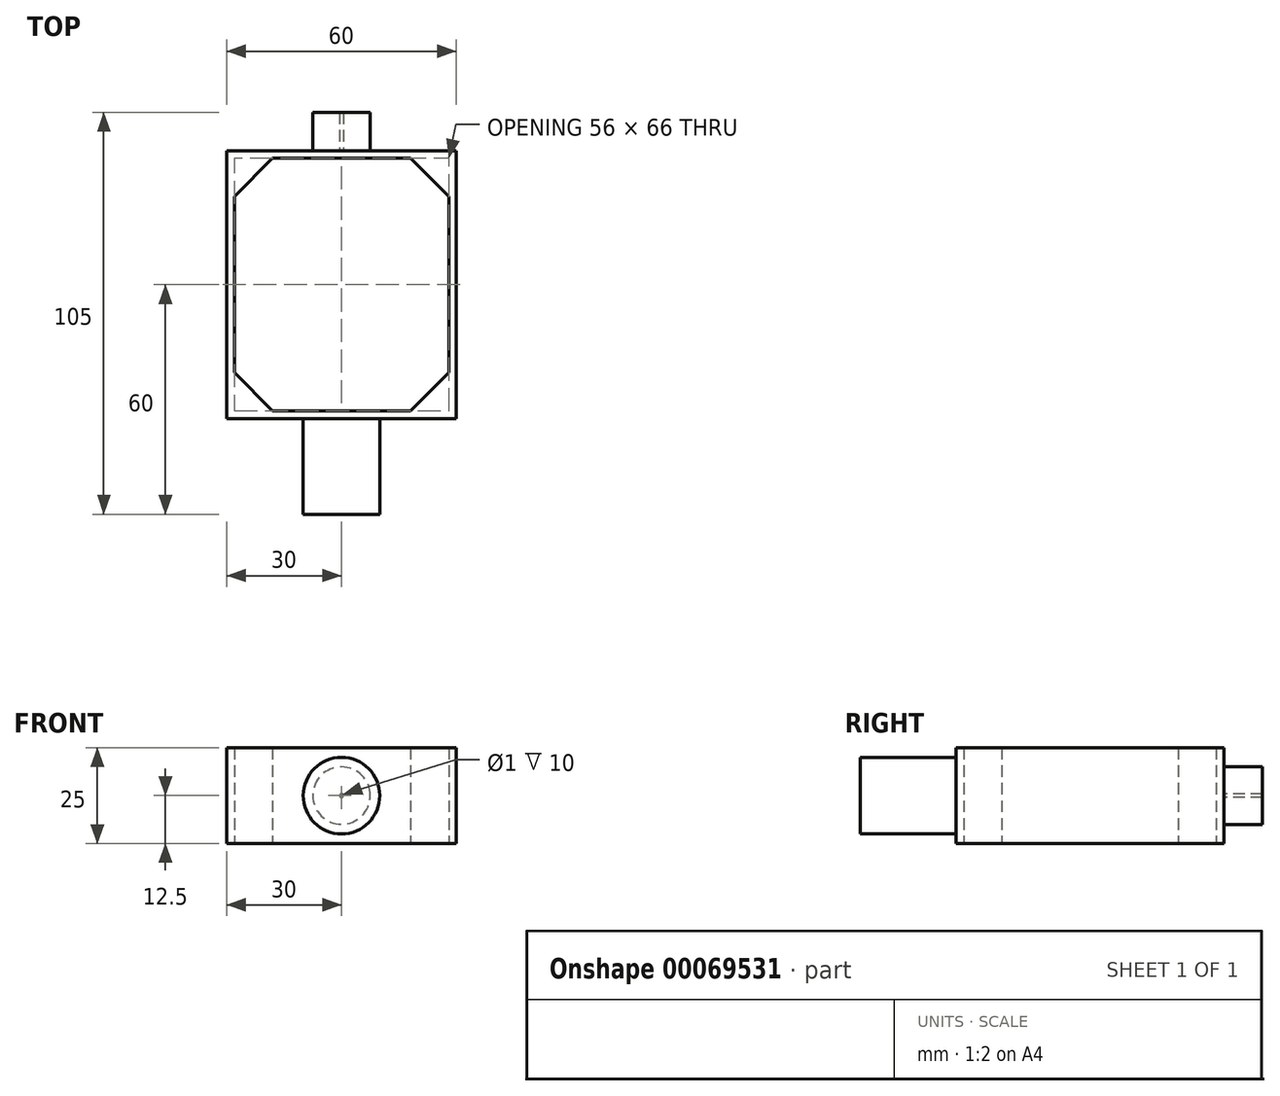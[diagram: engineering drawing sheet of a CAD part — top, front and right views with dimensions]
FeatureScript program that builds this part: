
annotation { "Feature Type Name" : "Feature", "Feature Type Description" : "" }
export const myFeature = defineFeature(function(context is Context, id is Id, definition is map)
    precondition{}
    {
        {
            var Q0;
            Q0=qCreatedBy(makeId("Top.planeOp"),FACE);
            var sketch = newSketch(context, id + "F0", { "sketchPlane" : qUnion([Q0])});
            skLineSegment(sketch, "E0.rect.bottom", {"start": v(-30, 35) * mm, "end": v(30, 35) * mm});
            skLineSegment(sketch, "E0.rect.top", {"start": v(-30, -35) * mm, "end": v(30, -35) * mm});
            skLineSegment(sketch, "E0.rect.left", {"start": v(-30, 35) * mm, "end": v(-30, -35) * mm});
            skLineSegment(sketch, "E0.rect.right", {"start": v(30, 35) * mm, "end": v(30, -35) * mm});
            skPoint(sketch, "E0.rect.middle", {"position": v(0, 0) * mm});
            skLineSegment(sketch, "E1.0", {"start": v(28, 23) * mm, "end": v(28, -23) * mm});
            skLineSegment(sketch, "E1.1", {"start": v(-18, 33) * mm, "end": v(18, 33) * mm});
            skLineSegment(sketch, "E1.2", {"start": v(-28, 23) * mm, "end": v(-28, -23) * mm});
            skLineSegment(sketch, "E1.3", {"start": v(-18, -33) * mm, "end": v(18, -33) * mm});
            skLineSegment(sketch, "E2", {"start": v(-28, -23) * mm, "end": v(-18, -33) * mm});
            skPoint(sketch, "E3.orphan", {"position": v(-28, -33) * mm});
            skLineSegment(sketch, "E4.MirrorCS", {"start": v(28, -23) * mm, "end": v(18, -33) * mm});
            skLineSegment(sketch, "E5", {"start": v(-5.44, 0) * mm, "end": v(7.4, 0) * mm});
            skLineSegment(sketch, "E6.MirrorCS", {"start": v(28, 23) * mm, "end": v(18, 33) * mm});
            skLineSegment(sketch, "E7.MirrorCS", {"start": v(-28, 23) * mm, "end": v(-18, 33) * mm});
            skSolve(sketch);
        }
        {
            var Q0;
            Q0 = qSketchRegion(id + "F0", true);
            extrude(context, id + "F1", {"entities" : qUnion([Q0]), "depth" : 25 * mm});
        }
        {
            var Q0;
            Q0=makeQuery(id+"F1.opExtrude","SWEPT_FACE",FACE,{"disambiguationData":[OSD([sQuery(id+"F0.wireOp",EDGE,"E0.rect.top")])]});
            var sketch = newSketch(context, id + "F2", { "sketchPlane" : qUnion([Q0])});
            skCircle(sketch, "E8", {"center": v(0, 12.5) * mm, "radius": 10 * mm});
            skSolve(sketch);
        }
        {
            var Q0;
            Q0 = qSketchRegion(id + "F2", true);
            extrude(context, id + "F3", {"entities" : qUnion([Q0]), "operationType" : NewBodyOperationType.ADD, "depth" : 25 * mm});
        }
        {
            var Q0;
            Q0=makeQuery(id+"F1.opExtrude","SWEPT_FACE",FACE,{"disambiguationData":[OSD([sQuery(id+"F0.wireOp",EDGE,"E0.rect.bottom")])]});
            var sketch = newSketch(context, id + "F4", { "sketchPlane" : qUnion([Q0])});
            skCircle(sketch, "E9", {"center": v(0, 12.5) * mm, "radius": 7.5 * mm});
            skCircle(sketch, "E10", {"center": v(0, 12.5) * mm, "radius": 0.5 * mm});
            skSolve(sketch);
        }
        {
            var Q0;
            Q0 = qSketchRegion(id + "F4", true);
            extrude(context, id + "F5", {"entities" : qUnion([Q0]), "operationType" : NewBodyOperationType.ADD, "depth" : 10 * mm});
        }
    });
